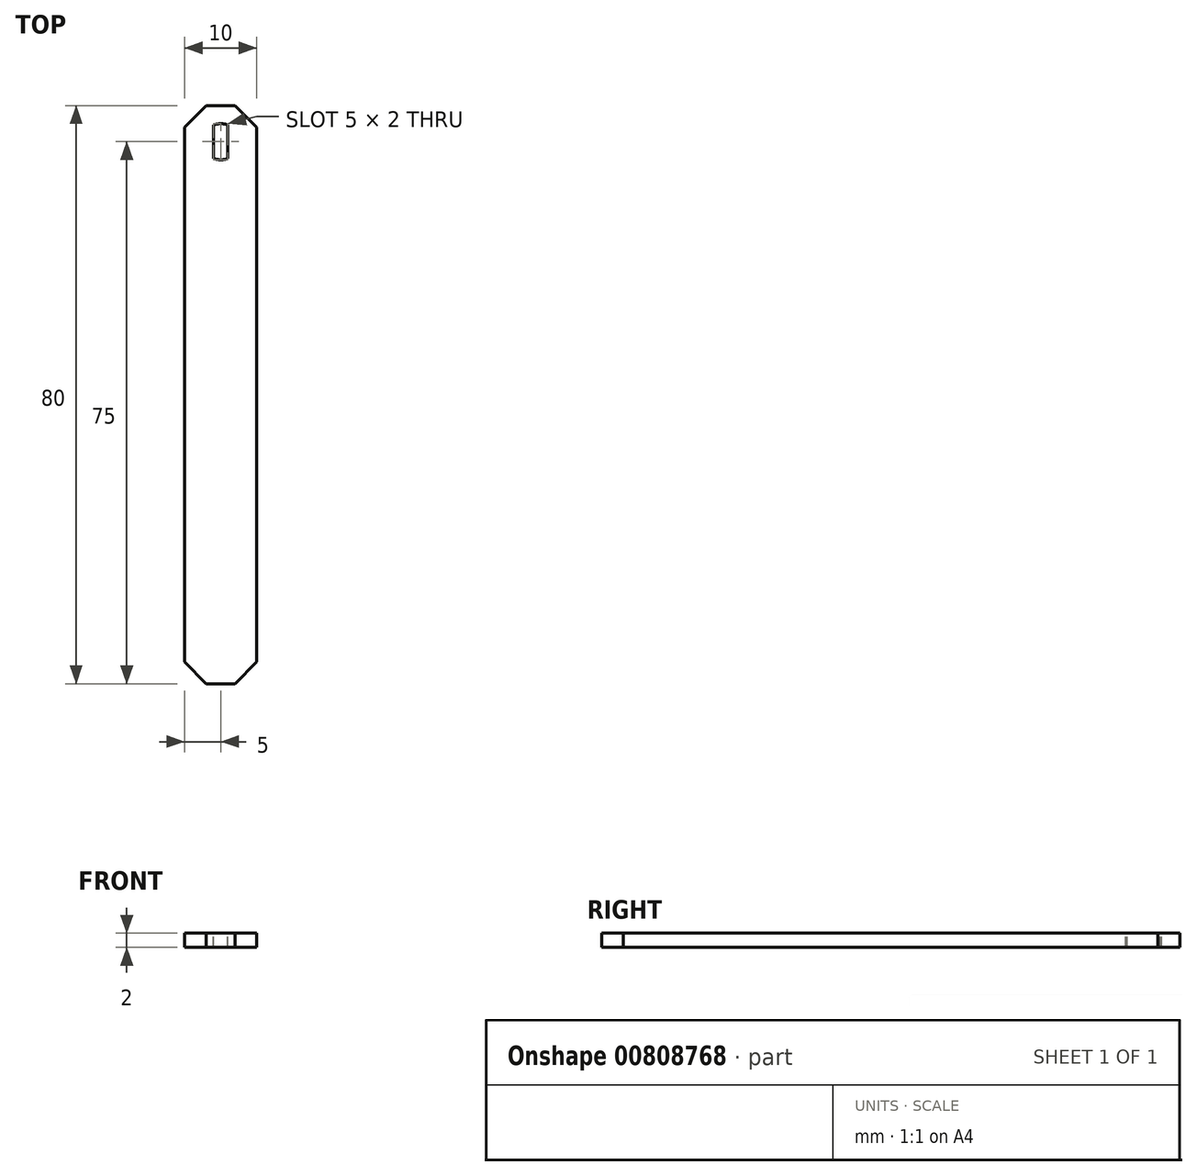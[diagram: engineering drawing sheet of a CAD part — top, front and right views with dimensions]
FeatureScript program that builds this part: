
annotation { "Feature Type Name" : "Feature", "Feature Type Description" : "" }
export const myFeature = defineFeature(function(context is Context, id is Id, definition is map)
    precondition{}
    {
        {
            var Q0;
            Q0=qCreatedBy(makeId("Front.planeOp"),FACE);
            var sketch = newSketch(context, id + "F0", { "sketchPlane" : qUnion([Q0])});
            skLineSegment(sketch, "E0.bottom", {"start": v(-5, 1) * mm, "end": v(5, 1) * mm});
            skLineSegment(sketch, "E0.top", {"start": v(-5, -1) * mm, "end": v(5, -1) * mm});
            skLineSegment(sketch, "E0.left", {"start": v(-5, 1) * mm, "end": v(-5, -1) * mm});
            skLineSegment(sketch, "E0.right", {"start": v(5, 1) * mm, "end": v(5, -1) * mm});
            skPoint(sketch, "E0.middle", {"position": v(0, 0) * mm});
            skSolve(sketch);
        }
        {
            var Q0;
            Q0 = qSketchRegion(id + "F0", true);
            extrude(context, id + "F1", {"entities" : qUnion([Q0]), "depth" : 80 * mm, "offsetDistance" : 25 * mm});
        }
        {
            var Q0;
            Q0=makeQuery(id+"F1.opExtrude","SWEPT_FACE",FACE,{"disambiguationData":[OSD([sQuery(id+"F0.wireOp",EDGE,"E0.bottom")])]});
            var sketch = newSketch(context, id + "F2", { "sketchPlane" : qUnion([Q0])});
            skArc(sketch, "E1", {"start": v(1, -2.7) * mm, "mid": v(0, -2.5) * mm, "end": v(-1, -2.7) * mm});
            skLineSegment(sketch, "E2.left", {"start": v(-1, -2.7) * mm, "end": v(-1, -7.3) * mm});
            skLineSegment(sketch, "E2.right", {"start": v(1, -2.7) * mm, "end": v(1, -7.3) * mm});
            skArc(sketch, "E3.trimOffspring", {"start": v(-1, -7.3) * mm, "mid": v(0, -7.5) * mm, "end": v(1, -7.3) * mm});
            skSolve(sketch);
        }
        {
            var Q0;
            Q0 = qSketchRegion(id + "F2", true);
            extrude(context, id + "F3", {"entities" : qUnion([Q0]), "operationType" : NewBodyOperationType.REMOVE, "endBound" : BoundingType.UP_TO_NEXT, "oppositeDirection" : true, "depth" : 3 * mm, "offsetDistance" : 25 * mm});
        }
        {
            var Q0;
            Q0=makeQuery(id+"F1.opExtrude","CAP_EDGE",EDGE,{"disambiguationData":[OSD([sQuery(id+"F0.wireOp",EDGE,"E0.left")])],"isStart":true});
            var Q1;
            Q1=makeQuery(id+"F1.opExtrude","CAP_EDGE",EDGE,{"disambiguationData":[OSD([sQuery(id+"F0.wireOp",EDGE,"E0.right")])],"isStart":true});
            var Q2;
            Q2=makeQuery(id+"F1.opExtrude","CAP_EDGE",EDGE,{"disambiguationData":[OSD([sQuery(id+"F0.wireOp",EDGE,"E0.left")])],"isStart":false});
            var Q3;
            Q3=makeQuery(id+"F1.opExtrude","CAP_EDGE",EDGE,{"disambiguationData":[OSD([sQuery(id+"F0.wireOp",EDGE,"E0.right")])],"isStart":false});
            chamfer(context, id + "F4", {"entities" : qUnion([Q0, Q1, Q2, Q3]), "width" : 3 * mm, "tangentPropagation" : true});
        }
    });
